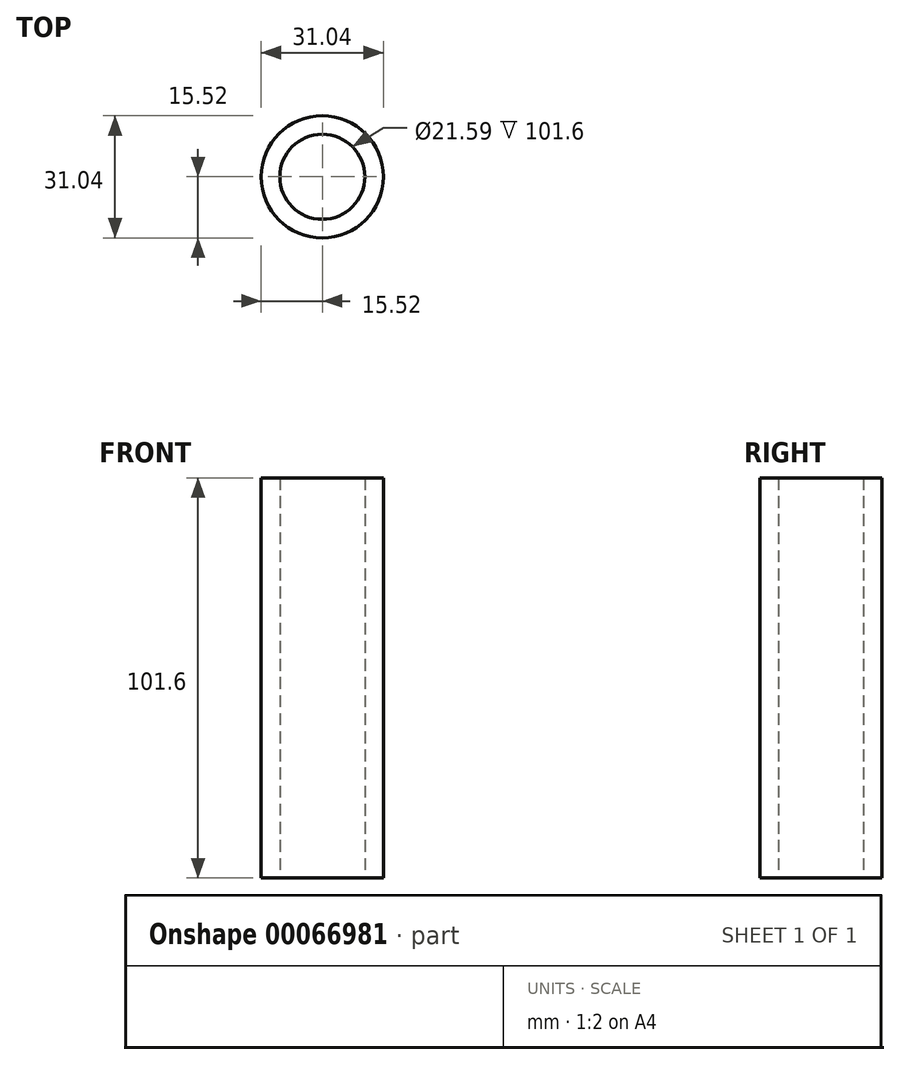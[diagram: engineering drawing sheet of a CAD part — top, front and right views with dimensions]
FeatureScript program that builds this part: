
annotation { "Feature Type Name" : "Feature", "Feature Type Description" : "" }
export const myFeature = defineFeature(function(context is Context, id is Id, definition is map)
    precondition{}
    {
        {
            var Q0;
            Q0=qCreatedBy(makeId("Top.planeOp"),FACE);
            var sketch = newSketch(context, id + "F0", { "sketchPlane" : qUnion([Q0])});
            skCircle(sketch, "E0", {"center": v(0, 0) * mm, "radius": 10.8 * mm});
            skCircle(sketch, "E1", {"center": v(0, 0) * mm, "radius": 15.52 * mm});
            skSolve(sketch);
        }
        {
            var Q0;
            Q0=makeQuery(id+"F0.imprint","IMPRINT",FACE,{"disambiguationData":[TD([[makeQuery(id+"F0.imprint","IMPRINT",EDGE,{"derivedFrom":sQuery(id+"F0.wireOp",EDGE,"E0")}),-1.0]])]});
            extrude(context, id + "F1", {"entities" : qUnion([Q0]), "depth" : 101.6 * mm});
        }
    });
